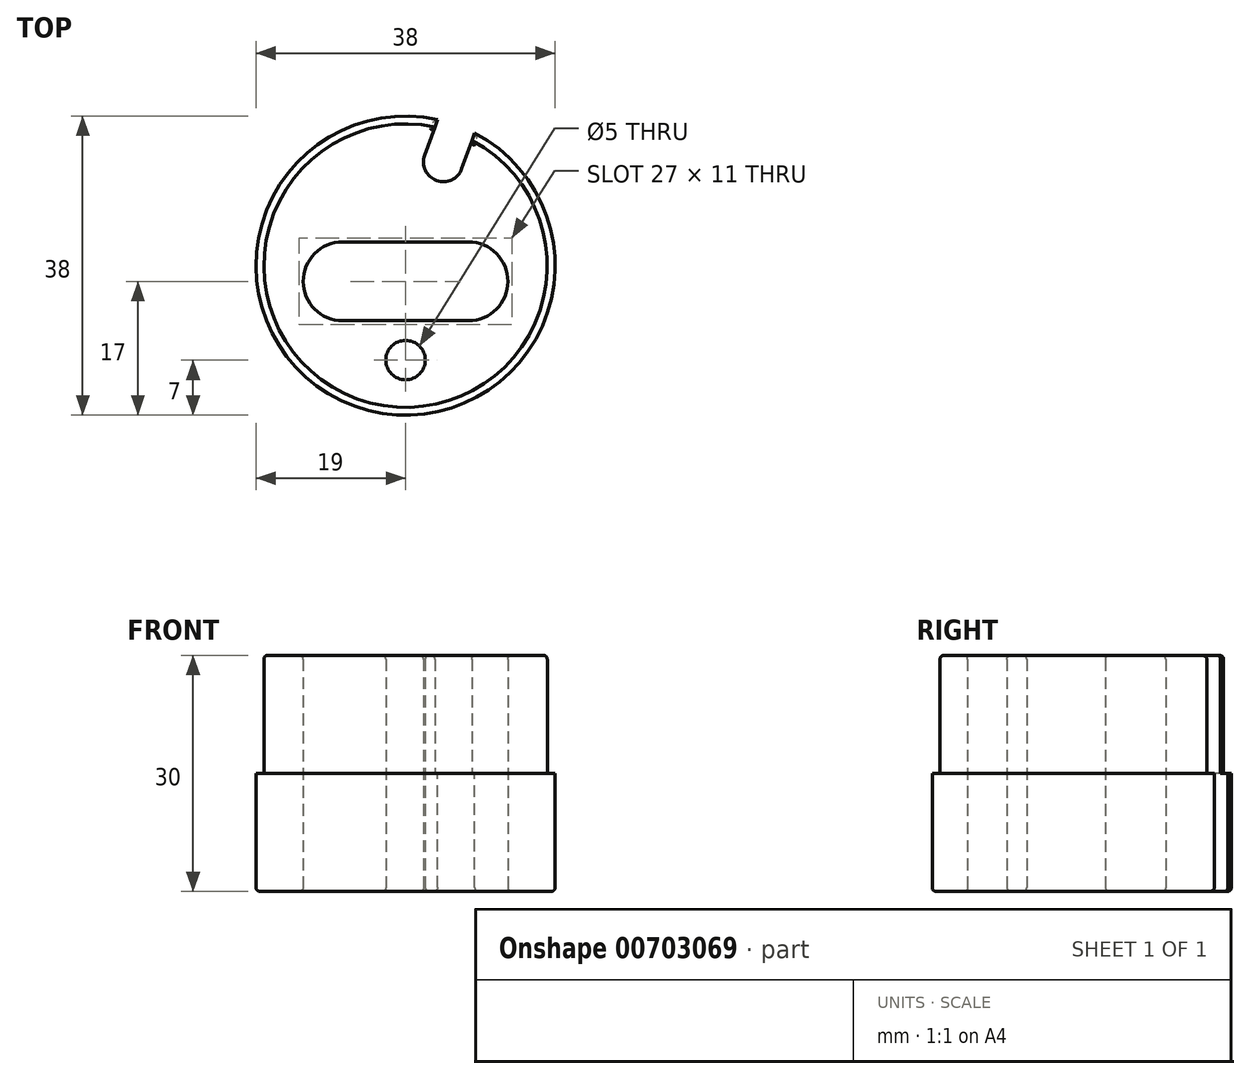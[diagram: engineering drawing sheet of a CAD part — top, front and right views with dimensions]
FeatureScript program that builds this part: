
annotation { "Feature Type Name" : "Feature", "Feature Type Description" : "" }
export const myFeature = defineFeature(function(context is Context, id is Id, definition is map)
    precondition{}
    {
        {
            var Q0;
            Q0=qCreatedBy(makeId("Top.planeOp"),FACE);
            var sketch = newSketch(context, id + "F0", { "sketchPlane" : qUnion([Q0])});
            skArc(sketch, "E0", {"start": v(4.1, 18.55) * mm, "mid": v(-6.5, -17.85) * mm, "end": v(8.8, 16.84) * mm});
            skArc(sketch, "E1", {"start": v(3.75, 17.6) * mm, "mid": v(-6.16, -16.91) * mm, "end": v(8.45, 15.9) * mm});
            skArc(sketch, "E2", {"start": v(-8, 3) * mm, "mid": v(-13, -2) * mm, "end": v(-8, -7) * mm});
            skArc(sketch, "E3", {"start": v(8, -7) * mm, "mid": v(13, -2) * mm, "end": v(8, 3) * mm});
            skCircle(sketch, "E4", {"center": v(0, -12) * mm, "radius": 2.5 * mm});
            skArc(sketch, "E5", {"start": v(2.44, 14.01) * mm, "mid": v(3.93, 10.8) * mm, "end": v(7.14, 12.3) * mm});
            skLineSegment(sketch, "E6", {"start": v(-8, 3) * mm, "end": v(8, 3) * mm});
            skLineSegment(sketch, "E7", {"start": v(-8, -7) * mm, "end": v(8, -7) * mm});
            skLineSegment(sketch, "E8", {"start": v(4.79, 13.16) * mm, "end": v(0, 0) * mm, "construction": true});
            skLineSegment(sketch, "E9", {"start": v(2.44, 14.01) * mm, "end": v(4.1, 18.55) * mm});
            skLineSegment(sketch, "E10", {"start": v(7.14, 12.3) * mm, "end": v(8.8, 16.84) * mm});
            skSolve(sketch);
        }
        {
            var Q0;
            {var subQ0=sQuery(id+"F0.wireOp",EDGE,"E1");Q0=makeQuery(id+"F0.imprint","IMPRINT",FACE,{"disambiguationData":[TD([[makeQuery(id+"F0.imprint","IMPRINT",EDGE,{"derivedFrom":subQ0}),1.0]])]});}
            var Q1;
            Q1=sQuery(id+"F0.wireOp",EDGE,"E0");
            extrude(context, id + "F1", {"entities" : qUnion([Q0]), "surfaceEntities" : qUnion([Q1]), "depth" : 15 * mm, "offsetDistance" : 25 * mm});
        }
        {
            var Q0;
            Q0 = qSketchRegion(id + "F0", true);
            extrude(context, id + "F2", {"entities" : qUnion([Q0]), "operationType" : NewBodyOperationType.ADD, "oppositeDirection" : true, "depth" : 15 * mm, "offsetDistance" : 25 * mm});
        }
        {
            var Q0;
            Q0=makeQuery(id+"F1.opExtrude","CAP_FACE",FACE,{"disambiguationData":[OSD([sQuery(id+"F0.wireOp",EDGE,"E1"),sQuery(id+"F0.wireOp",EDGE,"E2"),sQuery(id+"F0.wireOp",EDGE,"E3"),sQuery(id+"F0.wireOp",EDGE,"E4"),sQuery(id+"F0.wireOp",EDGE,"E5"),sQuery(id+"F0.wireOp",EDGE,"E6"),sQuery(id+"F0.wireOp",EDGE,"E7"),sQuery(id+"F0.wireOp",EDGE,"E9"),sQuery(id+"F0.wireOp",EDGE,"E10")])],"isStart":false});
            fillet(context, id + "F3", {"entities" : qUnion([Q0]), "radius" : .5 * mm, "tangentPropagation" : true, "allowEdgeOverflow" : false});
        }
        {
            var Q0;
            Q0=makeQuery(id+"F2.opExtrude","CAP_FACE",FACE,{"disambiguationData":[OSD([sQuery(id+"F0.wireOp",EDGE,"E0"),sQuery(id+"F0.wireOp",EDGE,"E2"),sQuery(id+"F0.wireOp",EDGE,"E3"),sQuery(id+"F0.wireOp",EDGE,"E4"),sQuery(id+"F0.wireOp",EDGE,"E5"),sQuery(id+"F0.wireOp",EDGE,"E6"),sQuery(id+"F0.wireOp",EDGE,"E7"),sQuery(id+"F0.wireOp",EDGE,"E9"),sQuery(id+"F0.wireOp",EDGE,"E10")])],"isStart":false});
            fillet(context, id + "F4", {"entities" : qUnion([Q0]), "radius" : .5 * mm, "tangentPropagation" : true, "allowEdgeOverflow" : false});
        }
    });
